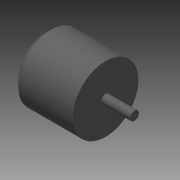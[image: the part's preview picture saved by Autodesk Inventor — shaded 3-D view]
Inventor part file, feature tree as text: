
AUTODESK INVENTOR PART (.ipt)
format: ipt  version: 2014 SP1 (Build 180222100, 222)  size: 95,744 bytes
history: native  units: in
note: dims shown in document units (in); Inventor stores cm internally (conversion verified against a paired STEP export)
features: revolve x1, chamfer x1, sketch x1
ambient origin geometry x8: Origin, YZ Plane, XZ Plane, XY Plane, X Axis, Y Axis, Z Axis, Center Point
bodies: Solid1 (feature_tree)
feature tree (3):
  revolve  "Revolution1"  [1 undecoded]
  chamfer  "Chamfer1"  Distance=0.1575in
  sketch  "Sketch1"  dims[d0=1.1614in d1=2.126in d2=0.1575in d3=1.0236in d4=90.0deg d5=0.2in d6=0.125in d7=45.0deg]
note: 1 required parameter value undecoded (feature->parameter linkage not recoverable at this tier; creation-order binding heuristic only, values carry confidence <= 0.55)
